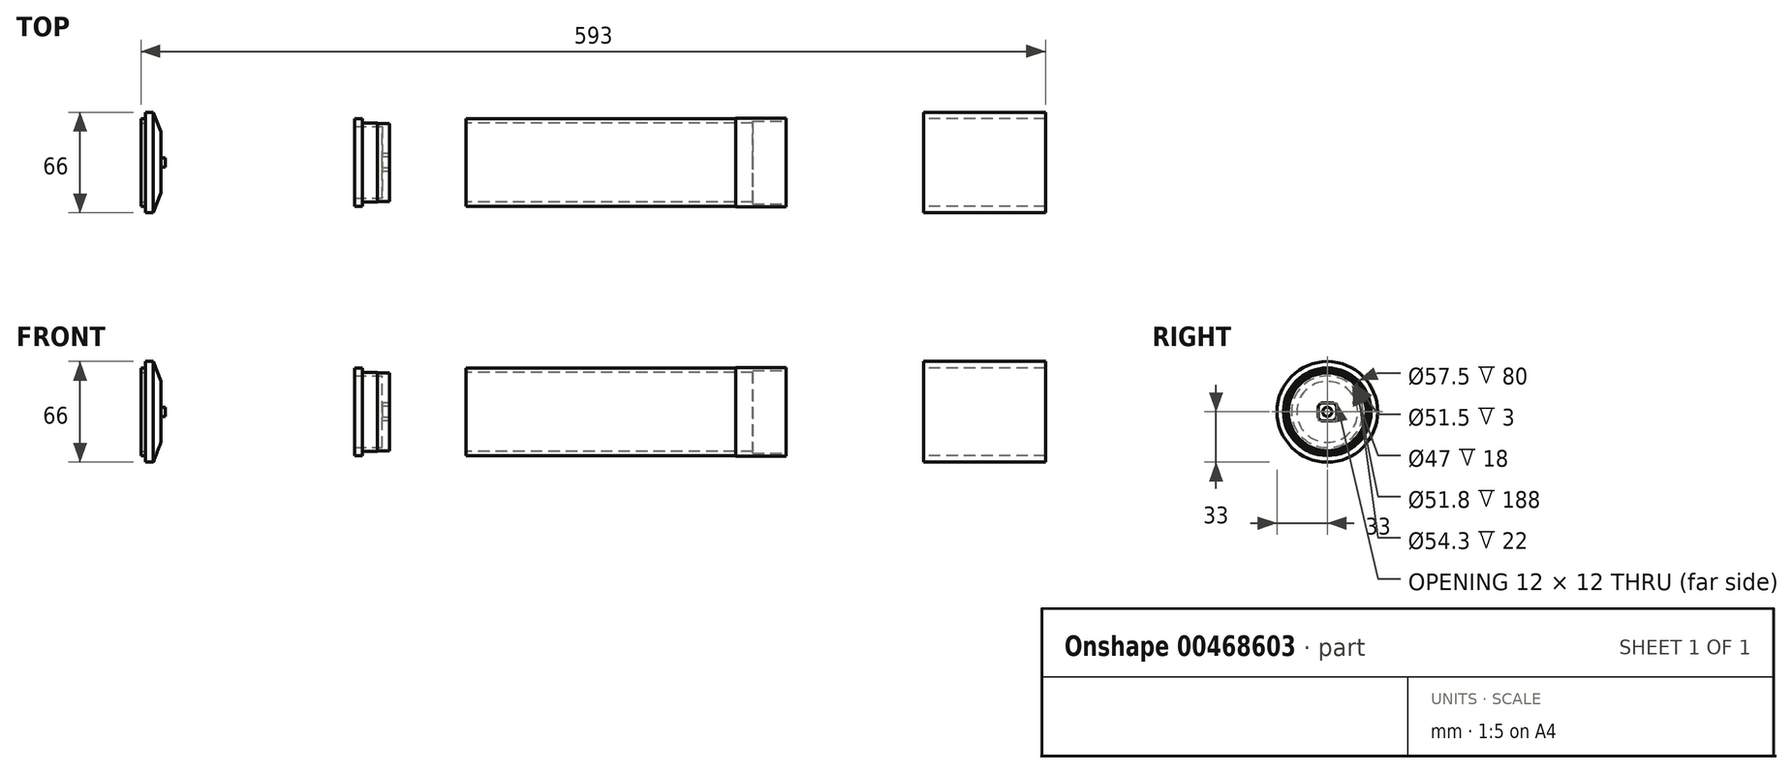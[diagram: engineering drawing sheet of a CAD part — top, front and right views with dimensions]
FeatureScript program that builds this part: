
annotation { "Feature Type Name" : "Feature", "Feature Type Description" : "" }
export const myFeature = defineFeature(function(context is Context, id is Id, definition is map)
    precondition{}
    {
        {
            var Q0;
            Q0=qCreatedBy(makeId("Front.planeOp"),FACE);
            var sketch = newSketch(context, id + "F0", { "sketchPlane" : qUnion([Q0])});
            skLineSegment(sketch, "E0", {"start": v(0, 0) * mm, "end": v(210, 0) * mm});
            skLineSegment(sketch, "E1", {"start": v(210, 0) * mm, "end": v(210, 25.9) * mm, "construction": true});
            skPoint(sketch, "E2", {"position": v(210, 29) * mm});
            skLineSegment(sketch, "E3", {"start": v(210, 29) * mm, "end": v(0, 29) * mm, "construction": true});
            skLineSegment(sketch, "E4", {"start": v(0, 29) * mm, "end": v(0, 0) * mm});
            skLineSegment(sketch, "E5", {"start": v(210, 25.9) * mm, "end": v(0, 25.9) * mm});
            skLineSegment(sketch, "E6", {"start": v(210, 29) * mm, "end": v(210, 25.9) * mm});
            skPoint(sketch, "E7", {"position": v(177, 29) * mm});
            skLineSegment(sketch, "E8", {"start": v(177, 29) * mm, "end": v(177, 28.75) * mm});
            skLineSegment(sketch, "E9", {"start": v(177, 28.75) * mm, "end": v(0, 28.75) * mm});
            skLineSegment(sketch, "E10", {"start": v(177, 29) * mm, "end": v(210, 29) * mm});
            skSolve(sketch);
        }
        {
            var Q0;
            Q0=qSketchRegion(id+"F0",true);
            var Q1;
            Q1=sQuery(id+"F0.wireOp",EDGE,"E0");
            revolve(context, id + "F1", {"entities" : qUnion([Q0]), "axis" : qUnion([Q1]), "revolveType" : RevolveType.FULL});
        }
        {
            var Q0;
            Q0=makeQuery(id+"F1.opRevolve","SWEPT_FACE",FACE,{"disambiguationData":[OSD([sQuery(id+"F0.wireOp",EDGE,"E6")])]});
            var sketch = newSketch(context, id + "F2", { "sketchPlane" : qUnion([Q0])});
            skCircle(sketch, "E11.0", {"center": v(0, 0) * mm, "radius": 25.9 * mm});
            skCircle(sketch, "E12", {"center": v(0, 0) * mm, "radius": 27.15 * mm});
            skSolve(sketch);
        }
        {
            var Q0;
            Q0=qSketchRegion(id+"F2",true);
            extrude(context, id + "F3", {"entities" : qUnion([Q0]), "operationType" : NewBodyOperationType.REMOVE, "oppositeDirection" : true, "depth" : 22 * mm});
        }
        {
            var Q0;
            Q0=qCreatedBy(makeId("Front.planeOp"),FACE);
            var sketch = newSketch(context, id + "F4", { "sketchPlane" : qUnion([Q0])});
            skLineSegment(sketch, "E13", {"start": v(0, 0) * mm, "end": v(-50, 0) * mm, "construction": true});
            skLineSegment(sketch, "E14", {"start": v(-50, 0) * mm, "end": v(-73, 0) * mm});
            skLineSegment(sketch, "E15", {"start": v(-73, 23.5) * mm, "end": v(-73, 28.75) * mm});
            skLineSegment(sketch, "E16", {"start": v(-73, 28.75) * mm, "end": v(-68, 28.75) * mm});
            skPoint(sketch, "E17", {"position": v(-68, 0) * mm});
            skPoint(sketch, "E18", {"position": v(-68, 26) * mm});
            skLineSegment(sketch, "E19", {"start": v(-68, 28.75) * mm, "end": v(-68, 26) * mm});
            skLineSegment(sketch, "E20", {"start": v(-68, 26) * mm, "end": v(-58, 26) * mm});
            skLineSegment(sketch, "E21", {"start": v(-58, 26) * mm, "end": v(-58, 25.5) * mm});
            skLineSegment(sketch, "E22", {"start": v(-58, 25.5) * mm, "end": v(-50, 25.5) * mm});
            skLineSegment(sketch, "E23", {"start": v(-50, 25.5) * mm, "end": v(-50, 0) * mm});
            skPoint(sketch, "E24", {"position": v(-73, 23.5) * mm});
            skLineSegment(sketch, "E25", {"start": v(-73, 23.5) * mm, "end": v(-55, 23.5) * mm});
            skLineSegment(sketch, "E26", {"start": v(-55, 23.5) * mm, "end": v(-55, 0) * mm});
            skSolve(sketch);
        }
        {
            var Q0;
            Q0=qSketchRegion(id+"F4",true);
            var Q1;
            Q1=sQuery(id+"F4.wireOp",EDGE,"E14");
            revolve(context, id + "F5", {"entities" : qUnion([Q0]), "axis" : qUnion([Q1]), "revolveType" : RevolveType.FULL});
        }
        {
            var Q0;
            Q0=makeQuery(id+"F5.opRevolve","SWEPT_FACE",FACE,{"disambiguationData":[OSD([sQuery(id+"F4.wireOp",EDGE,"E26")])]});
            var sketch = newSketch(context, id + "F6", { "sketchPlane" : qUnion([Q0])});
            skLineSegment(sketch, "E27.bottom", {"start": v(6, 6) * mm, "end": v(-6, 6) * mm});
            skLineSegment(sketch, "E27.top", {"start": v(6, -6) * mm, "end": v(-6, -6) * mm});
            skLineSegment(sketch, "E27.left", {"start": v(6, 6) * mm, "end": v(6, -6) * mm});
            skLineSegment(sketch, "E27.right", {"start": v(-6, 6) * mm, "end": v(-6, -6) * mm});
            skPoint(sketch, "E27.middle", {"position": v(0, 0) * mm});
            skCircle(sketch, "E28", {"center": v(0, 0) * mm, "radius": 7 * mm});
            skSolve(sketch);
        }
        {
            var Q0;
            {var subQ0=sQuery(id+"F6.wireOp",EDGE,"E28");var subQ10=sQuery(id+"F6.wireOp",EDGE,"E27.bottom");var subQ11=makeQuery(id+"F6.imprint","INTERSECT",VERTEX,{"disambiguationData":[OD(0.0)],"derivedFrom":[subQ10,subQ0]});Q0=makeQuery(id+"F6.imprint","IMPRINT",FACE,{"disambiguationData":[TD([[makeQuery(id+"F6.imprint","IMPRINT",EDGE,{"disambiguationData":[TD([[subQ11,-1.0]])],"derivedFrom":subQ10}),1.0]])]});}
            extrude(context, id + "F7", {"entities" : qUnion([Q0]), "operationType" : NewBodyOperationType.REMOVE, "oppositeDirection" : true, "depth" : 5 * mm});
        }
        {
            var Q0;
            Q0=qCreatedBy(makeId("Front.planeOp"),FACE);
            var sketch = newSketch(context, id + "F8", { "sketchPlane" : qUnion([Q0])});
            skLineSegment(sketch, "E29", {"start": v(0, 0) * mm, "end": v(300, 0) * mm, "construction": true});
            skLineSegment(sketch, "E30", {"start": v(300, 0) * mm, "end": v(300, 28.75) * mm});
            skPoint(sketch, "E31", {"position": v(300, 33) * mm});
            skLineSegment(sketch, "E32", {"start": v(300, 33) * mm, "end": v(380, 33) * mm});
            skLineSegment(sketch, "E33", {"start": v(380, 33) * mm, "end": v(380, 28.75) * mm});
            skLineSegment(sketch, "E34", {"start": v(380, 28.75) * mm, "end": v(300, 28.75) * mm});
            skLineSegment(sketch, "E35", {"start": v(300, 28.75) * mm, "end": v(300, 33) * mm});
            skSolve(sketch);
        }
        {
            var Q0;
            Q0=qSketchRegion(id+"F8",true);
            var Q1;
            Q1=sQuery(id+"F8.wireOp",EDGE,"E29");
            revolve(context, id + "F9", {"entities" : qUnion([Q0]), "axis" : qUnion([Q1]), "revolveType" : RevolveType.FULL});
        }
        {
            var Q0;
            Q0=qCreatedBy(makeId("Front.planeOp"),FACE);
            var sketch = newSketch(context, id + "F10", { "sketchPlane" : qUnion([Q0])});
            skLineSegment(sketch, "E36", {"start": v(0, 0) * mm, "end": v(-200, 0) * mm, "construction": true});
            skLineSegment(sketch, "E37", {"start": v(-200, 0) * mm, "end": v(-200, 20) * mm});
            skLineSegment(sketch, "E38", {"start": v(-200, 20) * mm, "end": v(-205, 20) * mm, "construction": true});
            skPoint(sketch, "E39", {"position": v(-205, 0) * mm});
            skPoint(sketch, "E40", {"position": v(-205, 33) * mm});
            skLineSegment(sketch, "E41", {"start": v(-205, 33) * mm, "end": v(-200, 20) * mm});
            skLineSegment(sketch, "E42", {"start": v(-205, 33) * mm, "end": v(-210, 33) * mm});
            skLineSegment(sketch, "E43", {"start": v(-210, 33) * mm, "end": v(-210, 0) * mm});
            skLineSegment(sketch, "E44", {"start": v(-210, 0) * mm, "end": v(-200, 0) * mm});
            skPoint(sketch, "E45", {"position": v(-210, 0) * mm});
            skPoint(sketch, "E46", {"position": v(-210, 28.75) * mm});
            skLineSegment(sketch, "E47", {"start": v(-210, 28.75) * mm, "end": v(-213, 28.75) * mm});
            skLineSegment(sketch, "E48", {"start": v(-213, 28.75) * mm, "end": v(-213, 25.75) * mm});
            skLineSegment(sketch, "E49", {"start": v(-213, 25.75) * mm, "end": v(-210, 25.75) * mm});
            skLineSegment(sketch, "E50", {"start": v(-200, 0) * mm, "end": v(-197, 0) * mm});
            skLineSegment(sketch, "E51", {"start": v(-197, 0) * mm, "end": v(-197, 3) * mm});
            skLineSegment(sketch, "E52", {"start": v(-197, 3) * mm, "end": v(-200, 3) * mm});
            skSolve(sketch);
        }
        {
            var Q0;
            Q0=qSketchRegion(id+"F10",true);
            var Q1;
            Q1=sQuery(id+"F10.wireOp",EDGE,"E36");
            revolve(context, id + "F11", {"entities" : qUnion([Q0]), "axis" : qUnion([Q1]), "revolveType" : RevolveType.FULL});
        }
    });
